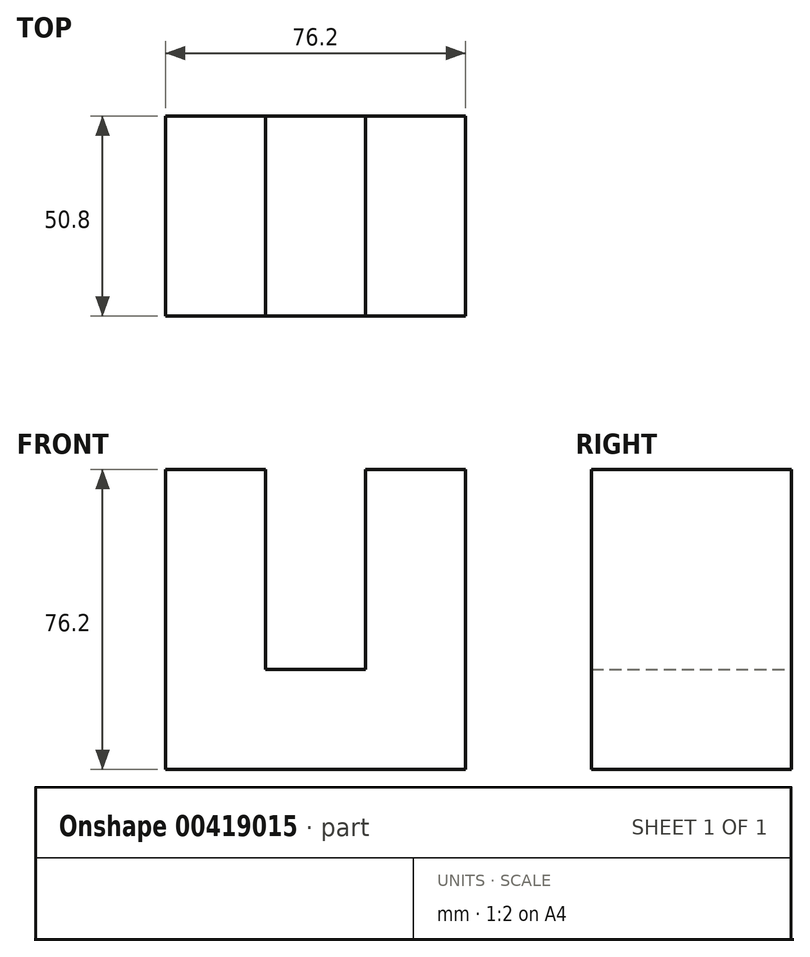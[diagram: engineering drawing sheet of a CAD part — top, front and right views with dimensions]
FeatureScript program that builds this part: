
annotation { "Feature Type Name" : "Feature", "Feature Type Description" : "" }
export const myFeature = defineFeature(function(context is Context, id is Id, definition is map)
    precondition{}
    {
        {
            var Q0;
            Q0=qCreatedBy(makeId("Front.planeOp"),FACE);
            var sketch = newSketch(context, id + "F0", { "sketchPlane" : qUnion([Q0])});
            skLineSegment(sketch, "E0", {"start": v(0, 0) * mm, "end": v(-76.2, 0) * mm});
            skLineSegment(sketch, "E1", {"start": v(-76.2, 0) * mm, "end": v(-76.2, 76.2) * mm});
            skLineSegment(sketch, "E2", {"start": v(-76.2, 76.2) * mm, "end": v(-50.8, 76.2) * mm});
            skLineSegment(sketch, "E3", {"start": v(-50.8, 76.2) * mm, "end": v(-50.8, 25.4) * mm});
            skLineSegment(sketch, "E4", {"start": v(0, 0) * mm, "end": v(0, 76.2) * mm});
            skLineSegment(sketch, "E5", {"start": v(0, 76.2) * mm, "end": v(-25.4, 76.2) * mm});
            skLineSegment(sketch, "E6", {"start": v(-25.4, 76.2) * mm, "end": v(-25.4, 25.4) * mm});
            skLineSegment(sketch, "E7", {"start": v(-25.4, 25.4) * mm, "end": v(-50.8, 25.4) * mm});
            skSolve(sketch);
        }
        {
            var Q0;
            Q0 = qSketchRegion(id + "F0", true);
            extrude(context, id + "F1", {"entities" : qUnion([Q0]), "depth" : 50.8 * mm});
        }
    });
